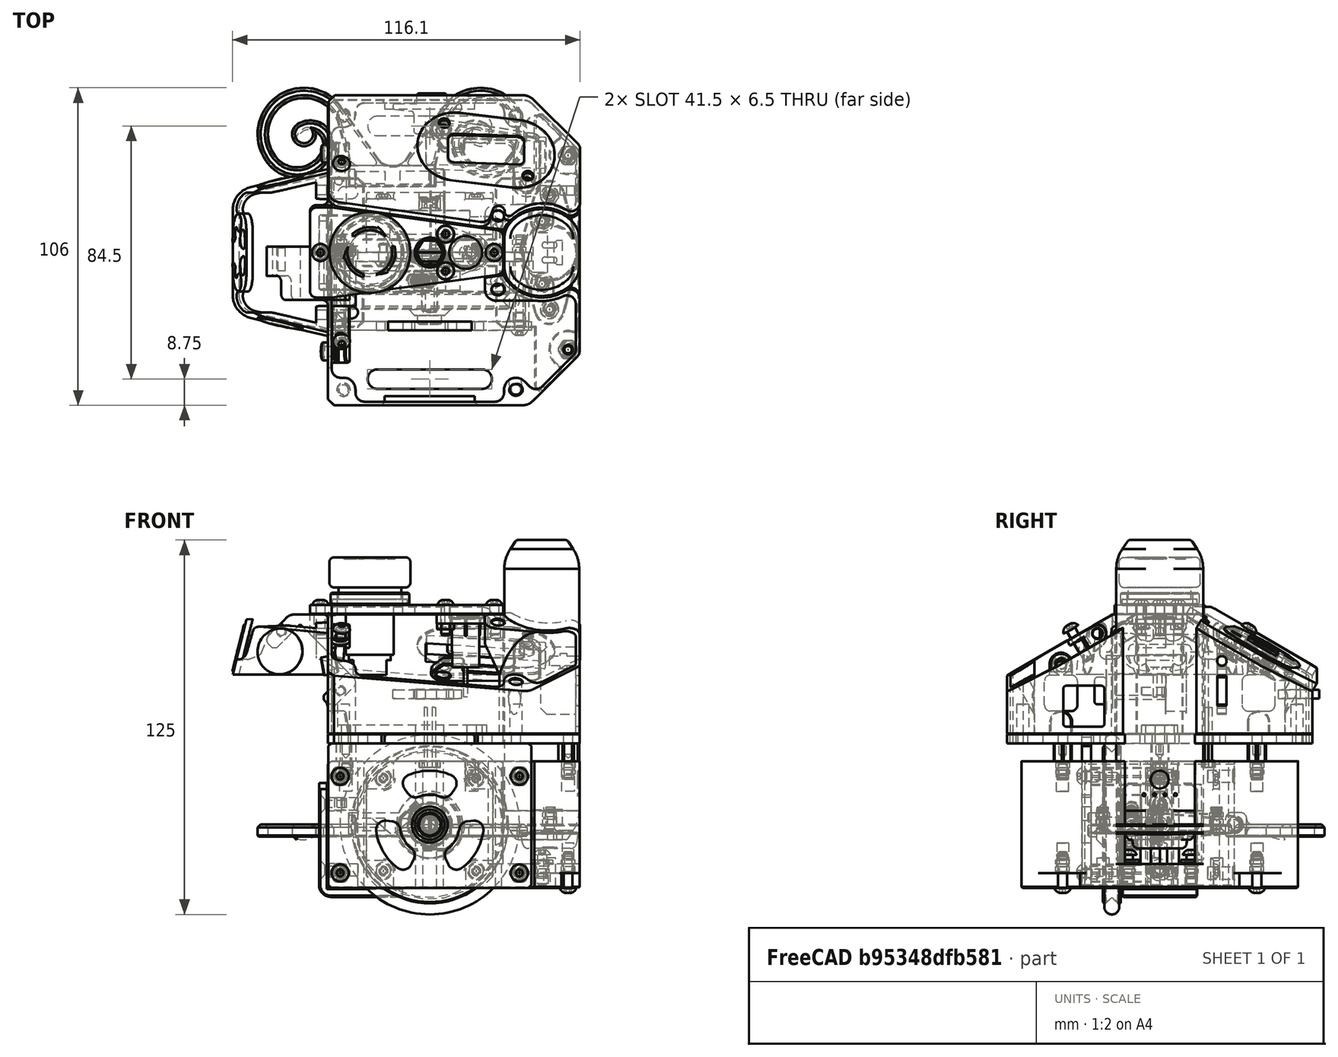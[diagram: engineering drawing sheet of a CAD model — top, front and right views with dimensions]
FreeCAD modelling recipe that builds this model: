
FCSTD DOCUMENT  (FreeCAD 2024.113R14555 (Git shallow))
Label: GridfinityBinPami
License: All rights reserved
LicenseURL: https://en.wikipedia.org/wiki/All_rights_reserved
objects: Part::Feature×86, App::Part×20, PartDesign::Fillet×8, Sketcher::SketchObject×7, PartDesign::Pad×6, App::Link×3, PartDesign::Chamfer×2, PartDesign::LinearPattern×2, PartDesign::Pocket×2, PartDesign::MultiTransform×1, PartDesign::Draft×1, PartDesign::Body×1
note: 167 computed .brp shape members not serialized (recipe doc carries the construction recipe); baked Part::Feature solids carry a one-line shape summary decoded from their .brp

FEATURE [Part::Feature] Solid  label="CarterSuperieur"
  FixShape = 1
  InvalidShape = false
  Placement = pos=(0,0,30.15) rot=(0,0,1;0rad)
  TreeRank = 7
  ValidateShape = false
  shape: bbox 104.5 x 102 x 40 mm, 286 faces (baked)
FEATURE [Part::Feature] Solid001  label="M4-Rondelle"
  FixShape = 1
  InvalidShape = false
  Placement = pos=(12,0,70.15) rot=(1,0,0;3.14159rad)
  TreeRank = 8
  ValidateShape = false
  shape: bbox 9 x 9 x 0.8 mm, 4 faces (baked)
FEATURE [Part::Feature] Solid002  label="TransferCarter"
  FixShape = 1
  InvalidShape = false
  TreeRank = 9
  ValidateShape = false
  shape: bbox 64.5 x 30 x 0.2 mm, 16 faces (baked)
FEATURE [Part::Feature] Solid003  label="BrideReed"
  FixShape = 1
  InvalidShape = false
  Placement = pos=(0,0,70.15) rot=(0,0,1;0rad)
  TreeRank = 10
  ValidateShape = false
  shape: bbox 16.01 x 18.3 x 3 mm, 13 faces (baked)
FEATURE [Part::Feature] Solid004  label="TopCarter"
  FixShape = 1
  InvalidShape = false
  Placement = pos=(0,0,70.35) rot=(0,0,1;0rad)
  TreeRank = 11
  ValidateShape = false
  shape: bbox 64.5 x 30 x 3 mm, 19 faces (baked)
FEATURE [Part::Feature] Solid005  label="BAU"
  FixShape = 1
  InvalidShape = false
  Placement = pos=(-20,0,56.7) rot=(0,0,1;0rad)
  TreeRank = 12
  ValidateShape = false
  shape: bbox 28.6 x 28.6 x 39.3 mm, 42 faces (baked)
FEATURE [Part::Feature] Solid006  label="ReedSensorShort"
  FixShape = 1
  InvalidShape = false
  Placement = pos=(12,0,69.15) rot=(0,0,1;0rad)
  TreeRank = 25
  ValidateShape = false
  shape: bbox 11 x 11 x 26.6 mm, 73 faces (baked)
FEATURE [Part::Feature] Solid007  label="BagueBAU"
  FixShape = 1
  InvalidShape = false
  Placement = pos=(-20,0,73.35) rot=(0,0,1;0rad)
  TreeRank = 26
  ValidateShape = false
  shape: bbox 26.25 x 26.25 x 4 mm, 8 faces (baked)
FEATURE [Part::Feature] Solid008  label="M3x10-Vis"
  FixShape = 1
  InvalidShape = false
  Placement = pos=(-36.5,0,73.35) rot=(0,0,1;0rad)
  TreeRank = 27
  ValidateShape = false
  shape: bbox 5.7 x 5.7 x 11.65 mm, 15 faces (baked)
FEATURE [Part::Feature] Solid009  label="M3x10-Vis004"
  FixShape = 1
  InvalidShape = false
  Placement = pos=(5.29088,-6.14799,73.35) rot=(0,0,1;0rad)
  TreeRank = 28
  ValidateShape = false
  shape: bbox 5.7 x 5.7 x 11.65 mm, 15 faces (baked)
FEATURE [Part::Feature] Solid010  label="M3x10-Vis005"
  FixShape = 1
  InvalidShape = false
  Placement = pos=(5.29088,6.14799,73.35) rot=(0,0,1;0rad)
  TreeRank = 29
  ValidateShape = false
  shape: bbox 5.7 x 5.7 x 11.65 mm, 15 faces (baked)
FEATURE [Part::Feature] Solid011  label="M3x10-Vis006"
  FixShape = 1
  InvalidShape = false
  Placement = pos=(21.5,0,73.35) rot=(0,0,1;0rad)
  TreeRank = 30
  ValidateShape = false
  shape: bbox 5.7 x 5.7 x 11.65 mm, 15 faces (baked)
FEATURE [Part::Feature] Solid012  label="M2.5-Écrou"
  FixShape = 1
  InvalidShape = false
  Placement = pos=(5.29088,6.14799,67.15) rot=(1,0,0;3.14159rad)
  TreeRank = 31
  ValidateShape = false
  shape: bbox 5.774 x 5.774 x 2 mm, 25 faces (baked)
FEATURE [Part::Feature] Solid013  label="M2.5-Écrou001"
  FixShape = 1
  InvalidShape = false
  Placement = pos=(5.29088,-6.14799,67.15) rot=(1,0,0;3.14159rad)
  TreeRank = 32
  ValidateShape = false
  shape: bbox 5.774 x 5.774 x 2 mm, 25 faces (baked)
FEATURE [App::Part] Part  label="VisserieIHM"
  ClaimAllChildren = false
  ExportMode = 1
  Group = -> [Solid008,Solid009,Solid010,Solid011,Solid012,Solid013]
  Origin = -> Origin
  TreeRank = 34
  _ExportChildren = -> [Solid008,Solid009,Solid010,Solid011,Solid012,Solid013]
  _GroupVersion = 1
FEATURE [App::Part] Part001  label="TopIHM"
  ClaimAllChildren = false
  ExportMode = 1
  Group = -> [Solid001,Solid002,Solid003,Solid004,Solid005,Solid006,Solid007,Part]
  Origin = -> Origin001
  TreeRank = 36
  _ExportChildren = -> [Solid001,Solid002,Solid003,Solid004,Solid005,Solid006,Solid007,Part]
  _GroupVersion = 1
FEATURE [Part::Feature] Solid014  label="Rotule"
  FixShape = 1
  InvalidShape = false
  Placement = pos=(-32.8,-20.8,63.8) rot=(1,0,0;0.523599rad)
  TreeRank = 49
  ValidateShape = false
  shape: bbox 6 x 13.59 x 8.169 mm, 29 faces (baked)
FEATURE [Part::Feature] Solid015  label="M3x12-Vis150"
  FixShape = 1
  InvalidShape = false
  Placement = pos=(-29.4979,-29.7083,65.2297) rot=(0.990394,0.138272,0;0.527788rad)
  TreeRank = 50
  ValidateShape = false
  shape: bbox 5.686 x 9.628 x 13.02 mm, 15 faces (baked)
FEATURE [Part::Feature] Solid016  label="M3x12-Vis151"
  FixShape = 1
  InvalidShape = false
  Placement = pos=(-29.4979,29.7083,65.2297) rot=(-0.990394,0.138272,0;0.527788rad)
  TreeRank = 51
  ValidateShape = false
  shape: bbox 5.686 x 9.628 x 13.02 mm, 15 faces (baked)
FEATURE [App::Part] Part002  label="VisserieAiles"
  ClaimAllChildren = false
  ExportMode = 1
  Group = -> [Solid015,Solid016]
  Origin = -> Origin002
  TreeRank = 53
  _ExportChildren = -> [Solid015,Solid016]
  _GroupVersion = 1
FEATURE [Part::Feature] Solid017  label="AileDroite"
  FixShape = 1
  InvalidShape = false
  TreeRank = 54
  ValidateShape = false
  shape: bbox 84.21 x 43.81 x 28.18 mm, 31 faces (baked)
FEATURE [Part::Feature] Solid018  label="CacheEcran"
  FixShape = 1
  InvalidShape = false
  TreeRank = 55
  ValidateShape = false
  shape: bbox 47.84 x 26.64 x 14.69 mm, 36 faces (baked)
FEATURE [Part::Feature] Solid019  label="SupportOled"
  FixShape = 1
  InvalidShape = false
  TreeRank = 56
  ValidateShape = false
  shape: bbox 36.56 x 26.07 x 14.38 mm, 50 faces (baked)
FEATURE [Part::Feature] Solid020  label="ProtectionEcran"
  FixShape = 1
  InvalidShape = false
  TreeRank = 57
  ValidateShape = false
  shape: bbox 45.85 x 25.07 x 13.51 mm, 8 faces (baked)
FEATURE [App::Part] Part003  label="Ailes"
  ClaimAllChildren = false
  ExportMode = 1
  Group = -> [Solid014,Part002,Solid017,Solid018,Solid019,Solid020]
  Origin = -> Origin003
  TreeRank = 59
  _ExportChildren = -> [Solid014,Part002,Solid017,Solid018,Solid019,Solid020]
  _GroupVersion = 1
FEATURE [Part::Feature] Solid021  label="HeadSupport"
  FixShape = 1
  InvalidShape = false
  Placement = pos=(-34,0,70.15) rot=(0,0,1;0rad)
  TreeRank = 60
  ValidateShape = false
  shape: bbox 32.13 x 55.71 x 20.11 mm, 132 faces (baked)
FEATURE [Part::Feature] Solid022  label="Transparent"
  FixShape = 1
  InvalidShape = false
  TreeRank = 76
  ValidateShape = false
  shape: bbox 20.45 x 4.4 x 19.2 mm, 15 faces (baked)
FEATURE [Part::Feature] Solid023  label="SupportColor"
  FixShape = 1
  InvalidShape = false
  TreeRank = 77
  ValidateShape = false
  shape: bbox 15 x 0.2 x 15 mm, 3 faces (baked)
FEATURE [Part::Feature] Solid024  label="Pupille"
  FixShape = 1
  InvalidShape = false
  Placement = pos=(0,-0.4,0.4) rot=(0,0,1;0rad)
  TreeRank = 78
  ValidateShape = false
  shape: bbox 10.82 x 0.8 x 10.82 mm, 4 faces (baked)
FEATURE [App::Part] Part004  label="Eye"
  ClaimAllChildren = false
  ExportMode = 1
  Group = -> [Solid022,Solid023,Solid024]
  Origin = -> Origin004
  Placement = pos=(-49.9835,-23.9284,57.8424) rot=(-0.357536,0.040736,-0.93301;0.243029rad)
  TreeRank = 80
  _ExportChildren = -> [Solid022,Solid023,Solid024]
  _GroupVersion = 1
FEATURE [App::Link] Link  label="Eye001"
  AutoLinkLabel = true
  AutoPlacement = true
  LinkPlacement = pos=(-49.9978,23.9423,57.839) rot=(0.025674,-0.037293,0.998975;3.39991rad)
  LinkedObject = -> Part004
  Placement = pos=(-49.9978,23.9423,57.839) rot=(0.025674,-0.037293,0.998975;3.39991rad)
  SyncGroupVisibility = false
  TreeRank = 81
  _LinkVersion = 1
FEATURE [Part::Feature] Solid025  label="BoutonInter"
  FixShape = 1
  InvalidShape = false
  Placement = pos=(-1.35,49.8,42.05) rot=(0,0,1;0rad)
  TreeRank = 82
  ValidateShape = false
  shape: bbox 23 x 13.5 x 3 mm, 30 faces (baked)
FEATURE [Part::Feature] Solid026  label="SpacerPCB"
  FixShape = 1
  InvalidShape = false
  Placement = pos=(0,0,30.2) rot=(0,0,1;0rad)
  TreeRank = 83
  ValidateShape = false
  shape: bbox 51.45 x 12 x 3.367 mm, 17 faces (baked)
FEATURE [Part::Feature] Solid027  label="DiffuseurLed"
  FixShape = 1
  InvalidShape = false
  TreeRank = 84
  ValidateShape = false
  shape: bbox 13 x 3 x 22.4 mm, 30 faces (baked)
FEATURE [Part::Feature] Solid028  label="Horn"
  FixShape = 1
  InvalidShape = false
  TreeRank = 85
  ValidateShape = false
  shape: bbox 5 x 32.81 x 10 mm, 27 faces (baked)
FEATURE [Part::Feature] Solid029  label="Antennas"
  FixShape = 1
  InvalidShape = false
  Placement = pos=(-12.5,25,0) rot=(0,0,1;0rad)
  TreeRank = 86
  ValidateShape = false
  shape: bbox 90 x 33 x 9.53 mm, 91 faces (baked)
FEATURE [App::Part] Part005  label="EnsembleAntennas"
  ClaimAllChildren = false
  ExportMode = 1
  Group = -> [Solid028,Solid029]
  Origin = -> Origin005
  Placement = pos=(-43.2,14,58.1) rot=(0.540716,0.540716,0.644401;1.99673rad)
  TreeRank = 88
  _ExportChildren = -> [Solid028,Solid029]
  _GroupVersion = 1
FEATURE [App::Part] Part006  label="ChassisSuperieur"
  ClaimAllChildren = false
  ExportMode = 1
  Group = -> [Solid,Part001,Part003,Solid021,Part004,Link,Solid025,Solid026,Solid027,Part005]
  Origin = -> Origin006
  TreeRank = 90
  _ExportChildren = -> [Solid,Part001,Part003,Solid021,Part004,Link,Solid025,Solid026,Solid027,Part005]
  _GroupVersion = 1
FEATURE [Part::Feature] Solid030  label="17HS08-1004S"
  FixShape = 1
  InvalidShape = false
  Placement = pos=(-2.4e-15,20,-4.4e-15) rot=(0,-0.707107,0.707107;3.14159rad)
  TreeRank = 100
  ValidateShape = false
  shape: bbox 42.32 x 40 x 62.15 mm, 316 faces (baked)
FEATURE [Part::Feature] Solid031  label="Roue60mm"
  FixShape = 1
  InvalidShape = false
  Placement = pos=(0,-6,0) rot=(0,0,1;0rad)
  TreeRank = 101
  ValidateShape = false
  shape: bbox 52.53 x 18 x 56.46 mm, 37 faces (baked)
FEATURE [Part::Feature] Solid032  label="JointTorique"
  FixShape = 1
  InvalidShape = false
  Placement = pos=(0,-16,0) rot=(0,0,1;0rad)
  TreeRank = 102
  ValidateShape = false
  shape: bbox 64.94 x 5 x 64.94 mm, 1 faces (baked)
FEATURE [Part::Feature] Solid033  label="M3-Insert004"
  FixShape = 1
  InvalidShape = false
  Placement = pos=(-1e-16,-9.5,-8.1) rot=(0.617822,0.786318,0;3.14159rad)
  TreeRank = 103
  ValidateShape = false
  shape: bbox 4.55 x 4.55 x 5.74 mm, 12 faces (baked)
FEATURE [Part::Feature] Solid034  label="M3-Insert005"
  FixShape = 1
  InvalidShape = false
  Placement = pos=(-5.72756,-9.5,5.72756) rot=(0,-1,0;0.785398rad)
  TreeRank = 104
  ValidateShape = false
  shape: bbox 7.032 x 4.55 x 7.032 mm, 12 faces (baked)
FEATURE [Part::Feature] Solid035  label="M3x3-Screw"
  FixShape = 1
  InvalidShape = false
  Placement = pos=(-5.72756,-9.5,5.72756) rot=(0,-1,0;0.785398rad)
  TreeRank = 105
  ValidateShape = false
  shape: bbox 3.677 x 3 x 3.677 mm, 14 faces (baked)
FEATURE [Part::Feature] Solid036  label="M3x3-Screw001"
  FixShape = 1
  InvalidShape = false
  Placement = pos=(0,-9.5,-8.1) rot=(1,0,0;3.14159rad)
  TreeRank = 106
  ValidateShape = false
  shape: bbox 3 x 3 x 3 mm, 14 faces (baked)
FEATURE [App::Part] Part007  label="VisserieRoue"
  ClaimAllChildren = false
  ExportMode = 1
  Group = -> [Solid033,Solid034,Solid035,Solid036]
  Origin = -> Origin007
  TreeRank = 108
  _ExportChildren = -> [Solid033,Solid034,Solid035,Solid036]
  _GroupVersion = 1
FEATURE [Part::Feature] Compound  label="CoreMF128"
  FixShape = 1
  InvalidShape = false
  TreeRank = 120
  ValidateShape = false
  shape: bbox 13.6 x 3.5 x 13.6 mm, 10 faces, 2 solids (baked)
FEATURE [Part::Feature] Solid037  label="SleeveMF128"
  FixShape = 1
  InvalidShape = false
  TreeRank = 121
  ValidateShape = false
  shape: bbox 11 x 3 x 11 mm, 4 faces (baked)
FEATURE [App::Part] Part008  label="MF128"
  ClaimAllChildren = false
  ExportMode = 1
  Group = -> [Compound,Solid037]
  Origin = -> Origin008
  Placement = pos=(0,-21.8,0) rot=(0,0,1;0rad)
  TreeRank = 123
  _ExportChildren = -> [Compound,Solid037]
  _GroupVersion = 1
FEATURE [App::Part] Part009  label="EnsembleRoue60mm"
  ClaimAllChildren = false
  ExportMode = 1
  Group = -> [Solid031,Solid032,Part007,Part008]
  Origin = -> Origin009
  Placement = pos=(0,-1.3,0) rot=(0,0,1;0rad)
  TreeRank = 125
  _ExportChildren = -> [Solid031,Solid032,Part007,Part008]
  _GroupVersion = 1
FEATURE [Part::Feature] Solid038  label="MotorPlate"
  FixShape = 1
  InvalidShape = false
  TreeRank = 126
  ValidateShape = false
  shape: bbox 67.84 x 3 x 42.3 mm, 19 faces (baked)
FEATURE [Part::Feature] Solid039  label="M3x20xx6-Standoff"
  FixShape = 1
  InvalidShape = false
  Placement = pos=(-29.9195,-3,16.15) rot=(1,0,0;1.5708rad)
  TreeRank = 127
  ValidateShape = false
  shape: bbox 6.582 x 25.9 x 6.17 mm, 30 faces (baked)
FEATURE [Part::Feature] Solid040  label="M3x20xx6-Standoff001"
  FixShape = 1
  InvalidShape = false
  Placement = pos=(29.9195,-3,16.15) rot=(1,0,0;1.5708rad)
  TreeRank = 128
  ValidateShape = false
  shape: bbox 6.582 x 25.9 x 6.17 mm, 30 faces (baked)
FEATURE [Part::Feature] Solid041  label="M3x20xx6-Standoff002"
  FixShape = 1
  InvalidShape = false
  Placement = pos=(29.9195,-3,-16.15) rot=(1,0,0;1.5708rad)
  TreeRank = 129
  ValidateShape = false
  shape: bbox 6.582 x 25.9 x 6.17 mm, 30 faces (baked)
FEATURE [Part::Feature] Solid042  label="M3x20xx6-Standoff003"
  FixShape = 1
  InvalidShape = false
  Placement = pos=(-29.9195,-3,-16.15) rot=(1,0,0;1.5708rad)
  TreeRank = 130
  ValidateShape = false
  shape: bbox 6.582 x 25.9 x 6.17 mm, 30 faces (baked)
FEATURE [Part::Feature] Solid043  label="M3-Insert"
  FixShape = 1
  InvalidShape = false
  Placement = pos=(29.9195,-3.6e-15,16.15) rot=(1,0,0;1.5708rad)
  TreeRank = 141
  ValidateShape = false
  shape: bbox 4.55 x 5.74 x 4.55 mm, 12 faces (baked)
FEATURE [Part::Feature] Solid044  label="M3-Insert001"
  FixShape = 1
  InvalidShape = false
  Placement = pos=(29.9195,3.6e-15,-16.15) rot=(1,0,0;1.5708rad)
  TreeRank = 142
  ValidateShape = false
  shape: bbox 4.55 x 5.74 x 4.55 mm, 12 faces (baked)
FEATURE [Part::Feature] Solid045  label="M3-Insert002"
  FixShape = 1
  InvalidShape = false
  Placement = pos=(-29.9195,-3.6e-15,16.15) rot=(1,0,0;1.5708rad)
  TreeRank = 143
  ValidateShape = false
  shape: bbox 4.55 x 5.74 x 4.55 mm, 12 faces (baked)
FEATURE [Part::Feature] Solid046  label="M3-Insert003"
  FixShape = 1
  InvalidShape = false
  Placement = pos=(-29.9195,3.6e-15,-16.15) rot=(1,0,0;1.5708rad)
  TreeRank = 144
  ValidateShape = false
  shape: bbox 4.55 x 5.74 x 4.55 mm, 12 faces (baked)
FEATURE [Part::Feature] Solid047  label="M3x6-Screw"
  FixShape = 1
  InvalidShape = false
  Placement = pos=(-29.9195,-26,16.15) rot=(1,0,0;1.5708rad)
  TreeRank = 145
  ValidateShape = false
  shape: bbox 5.7 x 7.65 x 5.7 mm, 15 faces (baked)
FEATURE [Part::Feature] Solid048  label="M3x6-Screw032"
  FixShape = 1
  InvalidShape = false
  Placement = pos=(-29.9195,-26,-16.15) rot=(1,0,0;1.5708rad)
  TreeRank = 146
  ValidateShape = false
  shape: bbox 5.7 x 7.65 x 5.7 mm, 15 faces (baked)
FEATURE [Part::Feature] Solid049  label="M3x6-Screw033"
  FixShape = 1
  InvalidShape = false
  Placement = pos=(29.9195,-26,-16.15) rot=(1,0,0;1.5708rad)
  TreeRank = 147
  ValidateShape = false
  shape: bbox 5.7 x 7.65 x 5.7 mm, 15 faces (baked)
FEATURE [Part::Feature] Solid050  label="M3x6-Screw034"
  FixShape = 1
  InvalidShape = false
  Placement = pos=(29.9195,-26,16.15) rot=(1,0,0;1.5708rad)
  TreeRank = 148
  ValidateShape = false
  shape: bbox 5.7 x 7.65 x 5.7 mm, 15 faces (baked)
FEATURE [Part::Feature] Solid051  label="M3x6-Screw007"
  FixShape = 1
  InvalidShape = false
  Placement = pos=(15.5,-3,15.5) rot=(1,0,0;1.5708rad)
  TreeRank = 149
  ValidateShape = false
  shape: bbox 5.7 x 7.65 x 5.7 mm, 15 faces (baked)
FEATURE [Part::Feature] Solid052  label="M3x6-Screw008"
  FixShape = 1
  InvalidShape = false
  Placement = pos=(15.5,-3,-15.5) rot=(1,0,0;1.5708rad)
  TreeRank = 150
  ValidateShape = false
  shape: bbox 5.7 x 7.65 x 5.7 mm, 15 faces (baked)
FEATURE [Part::Feature] Solid053  label="M3x6-Screw009"
  FixShape = 1
  InvalidShape = false
  Placement = pos=(-15.5,-3,-15.5) rot=(1,0,0;1.5708rad)
  TreeRank = 169
  ValidateShape = false
  shape: bbox 5.7 x 7.65 x 5.7 mm, 15 faces (baked)
FEATURE [Part::Feature] Solid054  label="M3x6-Screw010"
  FixShape = 1
  InvalidShape = false
  Placement = pos=(-15.5,-3,15.5) rot=(1,0,0;1.5708rad)
  TreeRank = 170
  ValidateShape = false
  shape: bbox 5.7 x 7.65 x 5.7 mm, 15 faces (baked)
FEATURE [App::Part] Part010  label="Visserie"
  ClaimAllChildren = false
  ExportMode = 1
  Group = -> [Solid039,Solid040,Solid041,Solid042,Solid043,Solid044,Solid045,Solid046,Solid047,Solid048,Solid049,Solid050,Solid051,Solid052,Solid053,Solid054]
  Origin = -> Origin010
  TreeRank = 172
  _ExportChildren = -> [Solid039,Solid040,Solid041,Solid042,Solid043,Solid044,Solid045,Solid046,Solid047,Solid048,Solid049,Solid050,Solid051,Solid052,Solid053,Solid054]
  _GroupVersion = 1
FEATURE [Part::Feature] Solid055  label="WheelPlate"
  FixShape = 1
  InvalidShape = false
  Placement = pos=(0,-23,0) rot=(0,0,1;0rad)
  TreeRank = 173
  ValidateShape = false
  shape: bbox 67.84 x 3 x 51.3 mm, 45 faces (baked)
FEATURE [App::Part] Part011  label="EnsemblePlate"
  ClaimAllChildren = false
  ExportMode = 1
  Group = -> [Solid038,Part010,Solid055]
  Origin = -> Origin011
  TreeRank = 175
  _ExportChildren = -> [Solid038,Part010,Solid055]
  _GroupVersion = 1
FEATURE [App::Part] Part012  label="EnsembleMoteurRoue"
  ClaimAllChildren = false
  ExportMode = 1
  Group = -> [Solid030,Part009,Part011]
  Origin = -> Origin012
  Placement = pos=(0,-25,0) rot=(0,0,1;0rad)
  TreeRank = 177
  _ExportChildren = -> [Solid030,Part009,Part011]
  _GroupVersion = 1
FEATURE [App::Link] Link001  label="EnsembleMoteurRoue001"
  AutoLinkLabel = true
  AutoPlacement = true
  LinkPlacement = pos=(-2.18557e-06,25,0) rot=(0,0,1;3.14159rad)
  LinkedObject = -> Part012
  Placement = pos=(-2.18557e-06,25,0) rot=(0,0,1;3.14159rad)
  SyncGroupVisibility = false
  TreeRank = 178
  _LinkVersion = 1
FEATURE [Part::Feature] Solid056  label="MainBody"
  FixShape = 1
  InvalidShape = false
  Placement = pos=(0,0,-21.15) rot=(0,0,1;0rad)
  TreeRank = 179
  ValidateShape = false
  shape: bbox 84 x 92.34 x 42.3 mm, 166 faces (baked)
FEATURE [Part::Feature] Solid057  label="M3x5.74-Insert"
  FixShape = 1
  InvalidShape = false
  Placement = pos=(46.2,32.426,-15.75) rot=(1,0,0;3.14159rad)
  TreeRank = 180
  ValidateShape = false
  shape: bbox 4.55 x 4.55 x 5.74 mm, 12 faces (baked)
FEATURE [Part::Feature] Solid058  label="M3x5.74-Insert066"
  FixShape = 1
  InvalidShape = false
  Placement = pos=(46.2,-32.426,-15.75) rot=(1,0,0;3.14159rad)
  TreeRank = 181
  ValidateShape = false
  shape: bbox 4.55 x 4.55 x 5.74 mm, 12 faces (baked)
FEATURE [Part::Feature] Solid059  label="Body097"
  FixShape = 1
  InvalidShape = false
  TreeRank = 182
  ValidateShape = false
  shape: bbox 4 x 10 x 10 mm, 12 faces (baked)
FEATURE [Part::Feature] Solid060  label="Body098"
  FixShape = 1
  InvalidShape = false
  TreeRank = 183
  ValidateShape = false
  shape: bbox 3.8 x 8 x 8 mm, 4 faces (baked)
FEATURE [App::Part] Part013  label="623ZZ"
  ClaimAllChildren = false
  ExportMode = 1
  Group = -> [Solid059,Solid060]
  Origin = -> Origin013
  Placement = pos=(46.2,-32.4,-17.15) rot=(0,1,0;1.5708rad)
  TreeRank = 185
  _ExportChildren = -> [Solid059,Solid060]
  _GroupVersion = 1
FEATURE [App::Link] Link002  label="623ZZ001"
  AutoLinkLabel = true
  AutoPlacement = true
  LinkPlacement = pos=(46.2,32.4,-17.15) rot=(0,1,0;1.5708rad)
  LinkedObject = -> Part013
  Placement = pos=(46.2,32.4,-17.15) rot=(0,1,0;1.5708rad)
  SyncGroupVisibility = false
  TreeRank = 186
  _LinkVersion = 1
FEATURE [Part::Feature] Solid061  label="M3x12-Vis"
  FixShape = 1
  InvalidShape = false
  Placement = pos=(46.2,-32.426,-21.15) rot=(1,0,0;3.14159rad)
  TreeRank = 199
  ValidateShape = false
  shape: bbox 5.7 x 5.7 x 13.65 mm, 15 faces (baked)
FEATURE [Part::Feature] Solid062  label="M3x12-Vis152"
  FixShape = 1
  InvalidShape = false
  Placement = pos=(46.2,32.426,-21.15) rot=(1,0,0;3.14159rad)
  TreeRank = 200
  ValidateShape = false
  shape: bbox 5.7 x 5.7 x 13.65 mm, 15 faces (baked)
FEATURE [App::Part] Part014  label="EnsembleRoulements"
  ClaimAllChildren = false
  ExportMode = 1
  Group = -> [Solid057,Solid058,Part013,Link002,Solid061,Solid062]
  Origin = -> Origin014
  TreeRank = 202
  _ExportChildren = -> [Solid057,Solid058,Part013,Link002,Solid061,Solid062]
  _GroupVersion = 1
FEATURE [Part::Feature] Solid063  label="SupportPatin"
  FixShape = 1
  InvalidShape = false
  TreeRank = 203
  ValidateShape = false
  shape: bbox 20 x 48 x 3 mm, 37 faces (baked)
FEATURE [Part::Feature] Solid064  label="Patin"
  FixShape = 1
  InvalidShape = false
  Placement = pos=(40,0,-3) rot=(0,0,1;0rad)
  TreeRank = 204
  ValidateShape = false
  shape: bbox 19.54 x 19.54 x 5 mm, 31 faces (baked)
FEATURE [Part::Feature] Solid065  label="M3x8-Vis"
  FixShape = 1
  InvalidShape = false
  Placement = pos=(40,-19,-3) rot=(1,0,0;3.14159rad)
  TreeRank = 205
  ValidateShape = false
  shape: bbox 6 x 6 x 8 mm, 16 faces (baked)
FEATURE [Part::Feature] Solid066  label="M3x8-Vis001"
  FixShape = 1
  InvalidShape = false
  Placement = pos=(40,19,-3) rot=(1,0,0;3.14159rad)
  TreeRank = 206
  ValidateShape = false
  shape: bbox 6 x 6 x 8 mm, 16 faces (baked)
FEATURE [Part::Feature] Solid067  label="M3x5.74-Insert010"
  FixShape = 1
  InvalidShape = false
  Placement = pos=(40,-19,0) rot=(1,0,0;3.14159rad)
  TreeRank = 207
  ValidateShape = false
  shape: bbox 4.55 x 4.55 x 5.74 mm, 12 faces (baked)
FEATURE [Part::Feature] Solid068  label="M3x5.74-Insert011"
  FixShape = 1
  InvalidShape = false
  Placement = pos=(40,19,0) rot=(1,0,0;3.14159rad)
  TreeRank = 208
  ValidateShape = false
  shape: bbox 4.55 x 4.55 x 5.74 mm, 12 faces (baked)
FEATURE [App::Part] Part015  label="EnsemblePatin"
  ClaimAllChildren = false
  ExportMode = 1
  Group = -> [Solid063,Solid064,Solid065,Solid066,Solid067,Solid068]
  Origin = -> Origin015
  Placement = pos=(0,0,-21.15) rot=(0,0,1;0rad)
  TreeRank = 210
  _ExportChildren = -> [Solid063,Solid064,Solid065,Solid066,Solid067,Solid068]
  _GroupVersion = 1
FEATURE [Part::Feature] Solid069  label="M3x5.74-Insert067"
  FixShape = 1
  InvalidShape = false
  Placement = pos=(46.2,-32.426,20.75) rot=(0,0,1;0rad)
  TreeRank = 221
  ValidateShape = false
  shape: bbox 4.55 x 4.55 x 5.74 mm, 12 faces (baked)
FEATURE [Part::Feature] Solid070  label="M3x5.74-Insert068"
  FixShape = 1
  InvalidShape = false
  Placement = pos=(46.2,32.426,20.75) rot=(0,0,1;0rad)
  TreeRank = 222
  ValidateShape = false
  shape: bbox 4.55 x 4.55 x 5.74 mm, 12 faces (baked)
FEATURE [Part::Feature] Solid071  label="M3x5.74-Insert069"
  FixShape = 1
  InvalidShape = false
  Placement = pos=(-28,0,20.75) rot=(0,0,1;0rad)
  TreeRank = 223
  ValidateShape = false
  shape: bbox 4.55 x 4.55 x 5.74 mm, 12 faces (baked)
FEATURE [Part::Feature] Solid072  label="M3x5.74-Insert070"
  FixShape = 1
  InvalidShape = false
  Placement = pos=(-33.6,0,-15.15) rot=(0,-1,0;1.5708rad)
  TreeRank = 224
  ValidateShape = false
  shape: bbox 5.74 x 4.55 x 4.55 mm, 12 faces (baked)
FEATURE [Part::Feature] Solid073  label="M3x5.74-Insert071"
  FixShape = 1
  InvalidShape = false
  Placement = pos=(-33.6,0,6.85) rot=(0,-1,0;1.5708rad)
  TreeRank = 225
  ValidateShape = false
  shape: bbox 5.74 x 4.55 x 4.55 mm, 12 faces (baked)
FEATURE [Part::Feature] Solid074  label="M3x6xx6-Entretoise filetéé"
  FixShape = 1
  InvalidShape = false
  Placement = pos=(46.2,-32.426,21.15) rot=(0,0,1;0rad)
  TreeRank = 226
  ValidateShape = false
  shape: bbox 6.582 x 6.17 x 11.9 mm, 30 faces (baked)
FEATURE [Part::Feature] Solid075  label="M3x6xx6-Entretoise filetéé001"
  FixShape = 1
  InvalidShape = false
  Placement = pos=(46.2,32.426,21.15) rot=(0,0,1;0rad)
  TreeRank = 227
  ValidateShape = false
  shape: bbox 6.582 x 6.17 x 11.9 mm, 30 faces (baked)
FEATURE [Part::Feature] Solid076  label="M3x6xx6-Entretoise filetéé002"
  FixShape = 1
  InvalidShape = false
  Placement = pos=(-28,0,21.15) rot=(0,0,1;0rad)
  TreeRank = 228
  ValidateShape = false
  shape: bbox 6.582 x 6.17 x 11.9 mm, 30 faces (baked)
FEATURE [Part::Feature] Solid077  label="M3x5.74-Insert072"
  FixShape = 1
  InvalidShape = false
  Placement = pos=(37.5,10.5,-12.2) rot=(0,0,1;0rad)
  TreeRank = 229
  ValidateShape = false
  shape: bbox 4.55 x 4.55 x 5.74 mm, 12 faces (baked)
FEATURE [Part::Feature] Solid078  label="M3x5.74-Insert073"
  FixShape = 1
  InvalidShape = false
  Placement = pos=(37.5,-10.5,-12.2) rot=(0,0,1;0rad)
  TreeRank = 230
  ValidateShape = false
  shape: bbox 4.55 x 4.55 x 5.74 mm, 12 faces (baked)
FEATURE [Part::Feature] Solid079  label="M3x5.74-Insert074"
  FixShape = 1
  InvalidShape = false
  Placement = pos=(14,0,20.75) rot=(0,0,1;0rad)
  TreeRank = 243
  ValidateShape = false
  shape: bbox 4.55 x 4.55 x 5.74 mm, 12 faces (baked)
FEATURE [Part::Feature] Solid080  label="M3x10-Vis007"
  FixShape = 1
  InvalidShape = false
  Placement = pos=(37.5,-10.5,-10.1) rot=(0,0,1;0rad)
  TreeRank = 244
  ValidateShape = false
  shape: bbox 5.7 x 5.7 x 11.65 mm, 15 faces (baked)
FEATURE [Part::Feature] Solid081  label="M3x10-Vis008"
  FixShape = 1
  InvalidShape = false
  Placement = pos=(37.5,10.5,-10.1) rot=(0,0,1;0rad)
  TreeRank = 245
  ValidateShape = false
  shape: bbox 5.7 x 5.7 x 11.65 mm, 15 faces (baked)
FEATURE [App::Part] Part016  label="VisserieBody"
  ClaimAllChildren = false
  ExportMode = 1
  Group = -> [Solid069,Solid070,Solid071,Solid072,Solid073,Solid074,Solid075,Solid076,Solid077,Solid078,Solid079,Solid080,Solid081]
  Origin = -> Origin016
  TreeRank = 247
  _ExportChildren = -> [Solid069,Solid070,Solid071,Solid072,Solid073,Solid074,Solid075,Solid076,Solid077,Solid078,Solid079,Solid080,Solid081]
  _GroupVersion = 1
FEATURE [Part::Feature] Solid082  label="TopPlate"
  FixShape = 1
  InvalidShape = false
  Placement = pos=(0,0,27.15) rot=(0,0,1;0rad)
  TreeRank = 248
  ValidateShape = false
  shape: bbox 84 x 102 x 3 mm, 69 faces (baked)
FEATURE [Part::Feature] Solid083  label="PowerBank-B0BHZ6RY6C"
  FixShape = 1
  InvalidShape = false
  Placement = pos=(37.4,4.7192e-06,-4.99999) rot=(0,0,1;1.5708rad)
  TreeRank = 249
  ValidateShape = false
  shape: bbox 25 x 29.49 x 100 mm, 94 faces (baked)
FEATURE [Part::Feature] Solid084  label="EquerreAvant"
  FixShape = 1
  InvalidShape = false
  Placement = pos=(-34,0,-21.15) rot=(0,0,1;0rad)
  TreeRank = 250
  ValidateShape = false
  shape: bbox 28 x 25 x 38 mm, 30 faces (baked)
FEATURE [App::Part] Part017  label="MotorisationPAMI-V2"
  ClaimAllChildren = false
  ExportMode = 1
  Group = -> [Part012,Link001,Solid056,Part014,Part015,Part016,Solid082,Solid083,Solid084]
  Origin = -> Origin017
  TreeRank = 252
  _ExportChildren = -> [Part012,Link001,Solid056,Part014,Part015,Part016,Solid082,Solid083,Solid084]
  _GroupVersion = 1
FEATURE [App::Part] Part018  label="Pami_2024"
  ClaimAllChildren = false
  ExportMode = 1
  Group = -> [Part006,Part017]
  Origin = -> Origin018
  Placement = pos=(54.5,63,37.3) rot=(0,0,1;3.14159rad)
  TreeRank = 254
  _ExportChildren = -> [Part006,Part017]
  _GroupVersion = 1
FEATURE [Sketcher::SketchObject] Sketch001
  ArcFitTolerance = 1e-06
  AttachmentSupport = -> [XY_Plane001]
  ExternalBSplineMaxDegree = 5
  ExternalBSplineTolerance = 0.0001
  FixShape = 1
  FullyConstrained = true
  InternalTolerance = 1e-06
  InvalidShape = false
  MakeInternals = false
  MapMode = 5
  Support = -> [XY_Plane001]
  TreeRank = 281
  ValidateShape = false
  sketch-geometry (11):
    g0: ArcOfCircle CenterX=4 CenterY=4 CenterZ=0 NormalX=0 NormalY=0 NormalZ=1 AngleXU=0 Radius=3.75 StartAngle=3.14159 EndAngle=4.71239
    g1: LineSegment StartX=0.25 StartY=4 StartZ=0 EndX=0.25 EndY=38 EndZ=0
    g2: ArcOfCircle CenterX=4 CenterY=38 CenterZ=0 NormalX=0 NormalY=0 NormalZ=1 AngleXU=0 Radius=3.75 StartAngle=1.5708 EndAngle=3.14159
    g3: LineSegment StartX=4 StartY=41.75 StartZ=0 EndX=38 EndY=41.75 EndZ=0
    g4: ArcOfCircle CenterX=38 CenterY=38 CenterZ=0 NormalX=0 NormalY=0 NormalZ=1 AngleXU=0 Radius=3.75 StartAngle=3e-16 EndAngle=1.5708
    g5: LineSegment StartX=41.75 StartY=38 StartZ=0 EndX=41.75 EndY=4 EndZ=0
    g6: ArcOfCircle CenterX=38 CenterY=4 CenterZ=0 NormalX=0 NormalY=0 NormalZ=1 AngleXU=0 Radius=3.75 StartAngle=4.71239 EndAngle=6.28319
    g7: LineSegment StartX=38 StartY=0.25 StartZ=0 EndX=4 EndY=0.25 EndZ=0
    g8: GeomPoint [constr] X=0.25 Y=0.25 Z=0
    g9: GeomPoint [constr] X=41.75 Y=41.75 Z=0
    g10: GeomPoint [constr] X=21 Y=21 Z=0
  constraints (25):
    c: Tangent(g0,g1) = 1.5708
    c: Tangent(g1,g2) = 1.5708
    c: Tangent(g2,g3) = 1.5708
    c: Tangent(g3,g4) = 1.5708
    c: Tangent(g4,g5) = 1.5708
    c: Tangent(g5,g6) = 1.5708
    c: Tangent(g6,g7) = 1.5708
    c: Tangent(g7,g0) = 1.5708
    c: Horizontal(g3)
    c: Horizontal(g7)
    c: Vertical(g1)
    c: Vertical(g5)
    c: Equal(g0,g2)
    c: Equal(g2,g4)
    c: Equal(g4,g6)
    c: PointOnObject(g8,g1)
    c: PointOnObject(g8,g7)
    c: PointOnObject(g9,g3)
    c: PointOnObject(g9,g5)
    c: Symmetric(g0,g4,g10)
    c: DistanceX(g-1,g10) = 21
    c: Equal(g7,g1)
    c: Radius(g6) = 3.75
    c: DistanceX(g0,g5) = 41.5
    c: DistanceY(g-1,g10) = 21
FEATURE [PartDesign::Pad] Pad001
  AddSubType = 0
  AlongSketchNormal = false
  AutoTaperInnerAngle = true
  CheckUpToFaceLimits = true
  ClaimChildren = false
  Direction = (0,0,1)
  Fit = 0
  FitJoin = 0
  FixShape = 1
  InnerFit = 0
  InnerFitJoin = 0
  InvalidShape = false
  Length = 4.4
  Length2 = 10
  Linearize = true
  NewSolid = false
  Profile = -> Sketch001
  ReferenceAxis = -> Sketch001 [N_Axis]
  Refine = true
  Reversed = true
  Suppress = false
  TaperInnerAngle = 0
  TaperInnerAngleRev = 0
  TreeRank = 282
  Type = 0
  ValidateShape = true
  _ProfileBasedVersion = 1
FEATURE [Sketcher::SketchObject] Sketch002
  ArcFitTolerance = 1e-06
  AttachmentSupport = -> [Pad001]
  ExternalBSplineMaxDegree = 5
  ExternalBSplineTolerance = 0.0001
  FixShape = 1
  FullyConstrained = true
  InternalTolerance = 1e-06
  InvalidShape = false
  MakeInternals = false
  MapMode = 5
  Placement = pos=(0,0,-4.4) rot=(1,0,0;3.14159rad)
  Support = -> [Pad001]
  TreeRank = 283
  ValidateShape = false
  sketch-geometry (11):
    g0: ArcOfCircle CenterX=4 CenterY=-4 CenterZ=0 NormalX=0 NormalY=0 NormalZ=1 AngleXU=0 Radius=1.6 StartAngle=1.5708 EndAngle=3.14159
    g1: LineSegment StartX=4 StartY=-2.4 StartZ=0 EndX=38 EndY=-2.4 EndZ=0
    g2: ArcOfCircle CenterX=38 CenterY=-4 CenterZ=0 NormalX=0 NormalY=0 NormalZ=1 AngleXU=0 Radius=1.6 StartAngle=0 EndAngle=1.5708
    g3: LineSegment StartX=39.6 StartY=-4 StartZ=0 EndX=39.6 EndY=-38 EndZ=0
    g4: ArcOfCircle CenterX=38 CenterY=-38 CenterZ=0 NormalX=0 NormalY=0 NormalZ=1 AngleXU=0 Radius=1.6 StartAngle=4.71239 EndAngle=6.28319
    g5: LineSegment StartX=38 StartY=-39.6 StartZ=0 EndX=4 EndY=-39.6 EndZ=0
    g6: ArcOfCircle CenterX=4 CenterY=-38 CenterZ=0 NormalX=0 NormalY=0 NormalZ=1 AngleXU=0 Radius=1.6 StartAngle=3.14159 EndAngle=4.71239
    g7: LineSegment StartX=2.4 StartY=-38 StartZ=0 EndX=2.4 EndY=-4 EndZ=0
    g8: GeomPoint [constr] X=2.4 Y=-2.4 Z=0
    g9: GeomPoint [constr] X=39.6 Y=-39.6 Z=0
    g10: GeomPoint [constr] X=21 Y=-21 Z=0
  constraints (25):
    c: Tangent(g0,g1) = 1.5708
    c: Tangent(g1,g2) = 1.5708
    c: Tangent(g2,g3) = 1.5708
    c: Tangent(g3,g4) = 1.5708
    c: Tangent(g4,g5) = 1.5708
    c: Tangent(g5,g6) = 1.5708
    c: Tangent(g6,g7) = 1.5708
    c: Tangent(g7,g0) = 1.5708
    c: Horizontal(g1)
    c: Horizontal(g5)
    c: Vertical(g3)
    c: Vertical(g7)
    c: Equal(g0,g2)
    c: Equal(g2,g4)
    c: Equal(g4,g6)
    c: PointOnObject(g8,g1)
    c: PointOnObject(g8,g7)
    c: PointOnObject(g9,g3)
    c: PointOnObject(g9,g5)
    c: Equal(g1,g3)
    c: Symmetric(g0,g4,g10)
    c: Radius(g2) = 1.6
    c: DistanceY(g10,g-1) = 21
    c: DistanceX(g-1,g10) = 21
    c: DistanceX(g0,g2) = 37.2
FEATURE [PartDesign::Pad] Pad002
  AddSubType = 0
  AlongSketchNormal = false
  AutoTaperInnerAngle = true
  BaseFeature = -> Pad001
  CheckUpToFaceLimits = true
  ClaimChildren = false
  Direction = (0,0,-1)
  Fit = 0
  FitJoin = 0
  FixShape = 1
  InnerFit = 0
  InnerFitJoin = 0
  InvalidShape = false
  Length = 2.6
  Length2 = 10
  Linearize = true
  NewSolid = false
  Profile = -> Sketch002
  ReferenceAxis = -> Sketch002 [N_Axis]
  Refine = true
  Suppress = false
  TaperInnerAngle = 0
  TaperInnerAngleRev = 0
  TreeRank = 284
  Type = 0
  ValidateShape = true
  _ProfileBasedVersion = 1
FEATURE [PartDesign::Chamfer] Chamfer
  AddSubType = 0
  Angle = 45
  Base = -> Pad002 [Edge37]
  BaseFeature = -> Pad002
  ChamferType = 0
  FixShape = 1
  FlipDirection = false
  InvalidShape = false
  NewSolid = false
  Refine = true
  Size = 0.8
  Size2 = 1
  SupportTransform = false
  Suppress = false
  TreeRank = 285
  UseAllEdges = false
  ValidateShape = true
FEATURE [PartDesign::Chamfer] Chamfer001
  AddSubType = 0
  Angle = 45
  Base = -> Chamfer [Edge15]
  BaseFeature = -> Chamfer
  ChamferType = 0
  FixShape = 1
  FlipDirection = false
  InvalidShape = false
  NewSolid = false
  Refine = true
  Size = 2.149
  Size2 = 1
  SupportTransform = false
  Suppress = false
  TreeRank = 286
  UseAllEdges = false
  ValidateShape = true
FEATURE [PartDesign::LinearPattern] LinearPattern
  AddSubType = 0
  CopyShape = false
  Direction = -> Sketch001 [H_Axis]
  FixShape = 1
  InvalidShape = false
  Length = 84
  NewSolid = false
  Occurrences = 3
  ParallelTransform = true
  Refine = true
  SubTransform = true
  Suppress = false
  TreeRank = 288
  ValidateShape = true
  _Version = 3
FEATURE [PartDesign::LinearPattern] LinearPattern001
  AddSubType = 0
  CopyShape = false
  Direction = -> Sketch001 [V_Axis]
  FixShape = 1
  InvalidShape = false
  Length = 84
  NewSolid = false
  Occurrences = 3
  ParallelTransform = true
  Refine = true
  SubTransform = true
  Suppress = false
  TreeRank = 289
  ValidateShape = true
  _Version = 3
FEATURE [PartDesign::MultiTransform] MultiTransform
  AddSubType = 0
  BaseFeature = -> Chamfer001
  CopyShape = false
  FixShape = 1
  InvalidShape = false
  NewSolid = false
  OriginalSubs = -> [Pad001,Pad002,Chamfer,Chamfer001]
  Originals = -> [Pad001,Pad002,Chamfer,Chamfer001]
  ParallelTransform = true
  Refine = true
  SubTransform = true
  Suppress = false
  Transformations = -> [LinearPattern,LinearPattern001]
  TreeRank = 287
  ValidateShape = true
  _Version = 3
FEATURE [Sketcher::SketchObject] Sketch003
  ArcFitTolerance = 1e-06
  AttachmentSupport = -> [XY_Plane001]
  ExternalBSplineMaxDegree = 5
  ExternalBSplineTolerance = 0.0001
  FixShape = 1
  FullyConstrained = true
  InternalTolerance = 1e-06
  InvalidShape = false
  MakeInternals = false
  MapMode = 5
  Support = -> [XY_Plane001]
  TreeRank = 290
  ValidateShape = false
  sketch-geometry (8):
    g0: LineSegment StartX=84 StartY=126 StartZ=0 EndX=126 EndY=126 EndZ=0
    g1: LineSegment StartX=126 StartY=126 StartZ=0 EndX=126 EndY=84 EndZ=0
    g2: LineSegment StartX=126 StartY=84 StartZ=0 EndX=84 EndY=84 EndZ=0
    g3: LineSegment StartX=84 StartY=84 StartZ=0 EndX=84 EndY=126 EndZ=0
    g4: LineSegment StartX=84 StartY=42 StartZ=0 EndX=126 EndY=42 EndZ=0
    g5: LineSegment StartX=126 StartY=42 StartZ=0 EndX=126 EndY=0 EndZ=0
    g6: LineSegment StartX=126 StartY=0 StartZ=0 EndX=84 EndY=0 EndZ=0
    g7: LineSegment StartX=84 StartY=0 StartZ=0 EndX=84 EndY=42 EndZ=0
  constraints (24):
    c: Coincident(g0,g1)
    c: Coincident(g1,g2)
    c: Coincident(g2,g3)
    c: Coincident(g3,g0)
    c: Horizontal(g0)
    c: Horizontal(g2)
    c: Vertical(g1)
    c: Vertical(g3)
    c: Coincident(g4,g5)
    c: Coincident(g5,g6)
    c: Coincident(g6,g7)
    c: Coincident(g7,g4)
    c: Horizontal(g4)
    c: Horizontal(g6)
    c: Vertical(g5)
    c: Vertical(g7)
    c: Equal(g4,g5)
    c: Equal(g5,g2)
    c: Equal(g2,g1)
    c: DistanceY(g1,g1) = 42
    c: PointOnObject(g5,g-1)
    c: PointOnObject(g4,g1)
    c: DistanceX(g-1,g5) = 126
    c: DistanceY(g5,g0) = 126
FEATURE [PartDesign::Pocket] Pocket
  AddSubType = 1
  AlongSketchNormal = false
  AutoTaperInnerAngle = true
  BaseFeature = -> MultiTransform
  CheckUpToFaceLimits = true
  ClaimChildren = false
  Direction = (0,0,-1)
  Fit = 0
  FitJoin = 0
  FixShape = 1
  InnerFit = 0
  InnerFitJoin = 0
  InvalidShape = false
  Length = 5
  Length2 = 10
  Linearize = true
  NewSolid = false
  Profile = -> Sketch003
  ReferenceAxis = -> Sketch003 [N_Axis]
  Refine = true
  Suppress = false
  TaperInnerAngle = 0
  TaperInnerAngleRev = 0
  TreeRank = 291
  Type = 1
  ValidateShape = true
  _ProfileBasedVersion = 1
  _Version = 1
FEATURE [Sketcher::SketchObject] Sketch004
  ArcFitTolerance = 1e-06
  AttachmentSupport = -> [XY_Plane001]
  ExternalBSplineMaxDegree = 5
  ExternalBSplineTolerance = 0.0001
  FixShape = 1
  FullyConstrained = true
  InternalTolerance = 1e-06
  InvalidShape = false
  MakeInternals = false
  MapMode = 5
  Support = -> [XY_Plane001]
  TreeRank = 292
  ValidateShape = false
  sketch-geometry (6):
    g0: LineSegment StartX=0 StartY=0 StartZ=0 EndX=0 EndY=126 EndZ=0
    g1: LineSegment StartX=0 StartY=126 StartZ=0 EndX=84 EndY=126 EndZ=0
    g2: LineSegment StartX=84 StartY=126 StartZ=0 EndX=126 EndY=84 EndZ=0
    g3: LineSegment StartX=126 StartY=84 StartZ=0 EndX=126 EndY=42 EndZ=0
    g4: LineSegment StartX=126 StartY=42 StartZ=0 EndX=84 EndY=0 EndZ=0
    g5: LineSegment StartX=84 StartY=0 StartZ=0 EndX=0 EndY=0 EndZ=0
  constraints (17):
    c: Coincident(g-1,g0)
    c: PointOnObject(g0,g-2)
    c: Coincident(g0,g1)
    c: Horizontal(g1)
    c: Coincident(g1,g2)
    c: Coincident(g2,g3)
    c: Vertical(g3)
    c: Coincident(g3,g4)
    c: PointOnObject(g4,g-1)
    c: Coincident(g4,g5)
    c: Coincident(g5,g0)
    c: DistanceY(g0,g0) = 126
    c: DistanceY(g3,g3) = 42
    c: DistanceX(g1,g1) = 84
    c: Equal(g5,g1)
    c: Equal(g4,g2)
    c: DistanceX(g0,g2) = 126
FEATURE [PartDesign::Pad] Pad003
  AddSubType = 0
  AlongSketchNormal = false
  AutoTaperInnerAngle = true
  BaseFeature = -> Pocket
  CheckUpToFaceLimits = true
  ClaimChildren = false
  Direction = (0,0,1)
  Fit = -0.1
  FitJoin = 0
  FixShape = 1
  InnerFit = 0
  InnerFitJoin = 0
  InvalidShape = false
  Length = 56
  Length2 = 10
  Linearize = true
  NewSolid = false
  Profile = -> Sketch004
  ReferenceAxis = -> Sketch004 [N_Axis]
  Refine = true
  Suppress = false
  TaperInnerAngle = 0
  TaperInnerAngleRev = 0
  TreeRank = 293
  Type = 0
  ValidateShape = true
  _ProfileBasedVersion = 1
FEATURE [PartDesign::Fillet] Fillet
  AddSubType = 0
  Base = -> Pad003 [Edge73,Edge74]
  BaseFeature = -> Pad003
  FixShape = 1
  InvalidShape = false
  NewSolid = false
  Radius = 4
  Refine = true
  SupportTransform = false
  Suppress = false
  TreeRank = 294
  UseAllEdges = false
  ValidateShape = true
FEATURE [PartDesign::Fillet] Fillet001
  AddSubType = 0
  Base = -> Fillet [Edge72,Edge76,Edge78,Edge74]
  BaseFeature = -> Fillet
  FixShape = 1
  InvalidShape = false
  NewSolid = false
  Radius = 9.5
  Refine = true
  SupportTransform = false
  Suppress = false
  TreeRank = 295
  UseAllEdges = false
  ValidateShape = true
FEATURE [PartDesign::Pocket] Pocket001
  AddSubType = 1
  AlongSketchNormal = false
  AutoTaperInnerAngle = true
  BaseFeature = -> Fillet001
  CheckUpToFaceLimits = true
  ClaimChildren = false
  Direction = (0,0,-1)
  Fit = -2
  FitJoin = 0
  FixShape = 1
  InnerFit = 0
  InnerFitJoin = 0
  InvalidShape = false
  Length = 53
  Length2 = 10
  Linearize = true
  NewSolid = false
  Profile = -> Fillet001 [Face70]
  Refine = true
  Suppress = false
  TaperInnerAngle = 0
  TaperInnerAngleRev = 0
  TreeRank = 296
  Type = 0
  ValidateShape = true
  _ProfileBasedVersion = 1
  _Version = 1
FEATURE [Sketcher::SketchObject] Sketch005
  ArcFitTolerance = 1e-06
  AttachmentSupport = -> [Pocket001]
  ExternalBSplineMaxDegree = 5
  ExternalBSplineTolerance = 0.0001
  FixShape = 1
  FullyConstrained = true
  InternalTolerance = 1e-06
  InvalidShape = false
  MakeInternals = false
  MapMode = 5
  Placement = pos=(0,0,3) rot=(0,0,1;0rad)
  Support = -> [Pocket001]
  TreeRank = 297
  ValidateShape = false
  sketch-geometry (6):
    g0: LineSegment StartX=2 StartY=103 StartZ=0 EndX=124 EndY=84 EndZ=0
    g1: LineSegment StartX=124 StartY=84 StartZ=0 EndX=124 EndY=42 EndZ=0
    g2: LineSegment StartX=124 StartY=42 StartZ=0 EndX=2 EndY=23 EndZ=0
    g3: LineSegment StartX=2 StartY=23 StartZ=0 EndX=2 EndY=103 EndZ=0
    g4: Circle CenterX=14.5 CenterY=63 CenterZ=0 NormalX=0 NormalY=0 NormalZ=1 AngleXU=0 Radius=11
    g5: Circle CenterX=76.5 CenterY=63 CenterZ=0 NormalX=0 NormalY=0 NormalZ=1 AngleXU=0 Radius=11
  constraints (18):
    c: Coincident(g0,g1)
    c: Coincident(g1,g2)
    c: Coincident(g2,g3)
    c: Coincident(g3,g0)
    c: Vertical(g1)
    c: Vertical(g3)
    c: DistanceY(g1,g1) = 42
    c: DistanceY(g1) = 42
    c: Equal(g0,g2)
    c: DistanceY(g3,g3) = 80
    c: Equal(g4,g5)
    c: Diameter(g4) = 22
    c: Horizontal(g4,g5)
    c: DistanceY(g4) = 63
    c: DistanceX(g4,g5) = 62
    c: DistanceX(g-1,g4) = 14.5
    c: DistanceX(g-1,g1) = 124
    c: DistanceX(g-1,g2) = 2
FEATURE [PartDesign::Pad] Pad004
  AddSubType = 0
  AlongSketchNormal = false
  AutoTaperInnerAngle = true
  BaseFeature = -> Pocket001
  CheckUpToFaceLimits = true
  ClaimChildren = false
  Direction = (0,0,1)
  Fit = 0
  FitJoin = 0
  FixShape = 1
  InnerFit = 0
  InnerFitJoin = 0
  InvalidShape = false
  Length = 10
  Length2 = 10
  Linearize = true
  NewSolid = false
  Profile = -> Sketch005
  ReferenceAxis = -> Sketch005 [N_Axis]
  Refine = true
  Suppress = false
  TaperInnerAngle = 0
  TaperInnerAngleRev = 0
  TreeRank = 298
  Type = 0
  ValidateShape = true
  _ProfileBasedVersion = 1
FEATURE [Sketcher::SketchObject] Sketch006
  ArcFitTolerance = 1e-06
  AttachmentSupport = -> [XY_Plane001]
  ExternalBSplineMaxDegree = 5
  ExternalBSplineTolerance = 0.0001
  ExternalGeometry = -> [Pad004]
  FixShape = 1
  FullyConstrained = true
  InternalTolerance = 1e-06
  InvalidShape = false
  MakeInternals = false
  MapMode = 5
  Support = -> [XY_Plane001]
  TreeRank = 299
  ValidateShape = false
  sketch-geometry (4):
    g0: LineSegment StartX=92 StartY=37.0164 StartZ=0 EndX=92 EndY=88.9836 EndZ=0
    g1: LineSegment StartX=92 StartY=88.9836 StartZ=0 EndX=124 EndY=84 EndZ=0
    g2: LineSegment StartX=124 StartY=84 StartZ=0 EndX=124 EndY=42 EndZ=0
    g3: LineSegment StartX=124 StartY=42 StartZ=0 EndX=92 EndY=37.0164 EndZ=0
  constraints (12):
    c: Vertical(g0)
    c: Coincident(g0,g1)
    c: Coincident(g1,g2)
    c: Vertical(g2)
    c: Coincident(g2,g3)
    c: Coincident(g3,g0)
    c: DistanceX(g-1,g2) = 124
    c: DistanceX(g0,g1) = 32
    c: PointOnObject(g1,g-3)
    c: PointOnObject(g0,g-3)
    c: PointOnObject(g2,g-4)
    c: PointOnObject(g0,g-4)
FEATURE [PartDesign::Pad] Pad005
  AddSubType = 0
  AlongSketchNormal = false
  AutoTaperInnerAngle = true
  BaseFeature = -> Pad004
  CheckUpToFaceLimits = true
  ClaimChildren = false
  Direction = (0,0,1)
  Fit = 0
  FitJoin = 0
  FixShape = 1
  InnerFit = 0
  InnerFitJoin = 0
  InvalidShape = false
  Length = 22
  Length2 = 10
  Linearize = true
  NewSolid = false
  Profile = -> Sketch006
  ReferenceAxis = -> Sketch006 [N_Axis]
  Refine = true
  Suppress = false
  TaperInnerAngle = 0
  TaperInnerAngleRev = 0
  TreeRank = 300
  Type = 0
  ValidateShape = true
  _ProfileBasedVersion = 1
FEATURE [PartDesign::Draft] Draft
  AddSubType = 0
  Angle = 10
  Base = -> Pad005 [Face30]
  BaseFeature = -> Pad005
  FixShape = 1
  InvalidShape = false
  NeutralPlane = -> Pad005 [Face28]
  NewSolid = false
  Refine = true
  SupportTransform = false
  Suppress = false
  TreeRank = 301
  ValidateShape = true
FEATURE [PartDesign::Fillet] Fillet002
  AddSubType = 0
  Base = -> Draft [Edge88]
  BaseFeature = -> Draft
  FixShape = 1
  InvalidShape = false
  NewSolid = false
  Radius = 5
  Refine = true
  SupportTransform = false
  Suppress = false
  TreeRank = 302
  UseAllEdges = false
  ValidateShape = true
FEATURE [PartDesign::Fillet] Fillet003
  AddSubType = 0
  Base = -> Fillet002 [Edge29]
  BaseFeature = -> Fillet002
  FixShape = 1
  InvalidShape = false
  NewSolid = false
  Radius = 1
  Refine = true
  SupportTransform = false
  Suppress = false
  TreeRank = 303
  UseAllEdges = false
  ValidateShape = true
FEATURE [PartDesign::Fillet] Fillet004
  AddSubType = 0
  Base = -> Fillet003 [Edge18,Edge19,Edge41,Edge43]
  BaseFeature = -> Fillet003
  FixShape = 1
  InvalidShape = false
  NewSolid = false
  Radius = 1
  Refine = true
  SupportTransform = false
  Suppress = false
  TreeRank = 304
  UseAllEdges = false
  ValidateShape = true
FEATURE [Sketcher::SketchObject] Sketch007
  ArcFitTolerance = 1e-06
  AttachmentSupport = -> [XY_Plane001]
  ExternalBSplineMaxDegree = 5
  ExternalBSplineTolerance = 0.0001
  ExternalGeometry = -> [Fillet004]
  FixShape = 1
  FullyConstrained = true
  InternalTolerance = 1e-06
  InvalidShape = false
  MakeInternals = false
  MapMode = 5
  Support = -> [XY_Plane001]
  TreeRank = 305
  ValidateShape = false
  sketch-geometry (4):
    g0: LineSegment StartX=29 StartY=98.7951 StartZ=0 EndX=29 EndY=27.2049 EndZ=0
    g1: LineSegment StartX=62 StartY=93.6557 StartZ=0 EndX=62 EndY=32.3443 EndZ=0
    g2: LineSegment StartX=29 StartY=98.7951 StartZ=0 EndX=62 EndY=93.6557 EndZ=0
    g3: LineSegment StartX=62 StartY=32.3443 StartZ=0 EndX=29 EndY=27.2049 EndZ=0
  constraints (12):
    c: Vertical(g0)
    c: Vertical(g1)
    c: Coincident(g2,g0)
    c: Coincident(g3,g1)
    c: Coincident(g3,g0)
    c: Coincident(g1,g2)
    c: DistanceX(g-1,g0) = 29
    c: DistanceX(g-1,g1) = 62
    c: PointOnObject(g1,g-4)
    c: PointOnObject(g1,g-3)
    c: PointOnObject(g0,g-3)
    c: PointOnObject(g0,g-4)
FEATURE [PartDesign::Pad] Pad006
  AddSubType = 0
  AlongSketchNormal = false
  AutoTaperInnerAngle = true
  BaseFeature = -> Fillet004
  CheckUpToFaceLimits = true
  ClaimChildren = false
  Direction = (0,0,1)
  Fit = 0
  FitJoin = 0
  FixShape = 1
  InnerFit = 0
  InnerFitJoin = 0
  InvalidShape = false
  Length = 16
  Length2 = 10
  Linearize = true
  NewSolid = false
  Profile = -> Sketch007
  ReferenceAxis = -> Sketch007 [N_Axis]
  Refine = true
  Suppress = false
  TaperInnerAngle = 0
  TaperInnerAngleRev = 0
  TreeRank = 306
  Type = 0
  ValidateShape = true
  _ProfileBasedVersion = 1
FEATURE [PartDesign::Fillet] Fillet005
  AddSubType = 0
  Base = -> Pad006 [Edge15,Edge34,Edge7,Edge10]
  BaseFeature = -> Pad006
  FixShape = 1
  InvalidShape = false
  NewSolid = false
  Radius = 1
  Refine = true
  SupportTransform = false
  Suppress = false
  TreeRank = 307
  UseAllEdges = false
  ValidateShape = true
FEATURE [PartDesign::Fillet] Fillet006
  AddSubType = 0
  Base = -> Fillet005 [Edge12,Edge32]
  BaseFeature = -> Fillet005
  FixShape = 1
  InvalidShape = false
  NewSolid = false
  Radius = 1
  Refine = true
  SupportTransform = false
  Suppress = false
  TreeRank = 308
  UseAllEdges = false
  ValidateShape = true
FEATURE [PartDesign::Fillet] Fillet007
  AddSubType = 0
  Base = -> Fillet006 [Edge3,Edge28]
  BaseFeature = -> Fillet006
  FixShape = 1
  InvalidShape = false
  NewSolid = false
  Radius = 4
  Refine = true
  SupportTransform = false
  Suppress = false
  TreeRank = 309
  UseAllEdges = false
  ValidateShape = true
FEATURE [PartDesign::Body] Body001  label="BinPami"
  AutoGroupSolids = false
  ClaimAllChildren = false
  ExportMode = 0
  FixShape = 1
  Group = -> [Sketch001,Pad001,Sketch002,Pad002,Chamfer,Chamfer001,MultiTransform,LinearPattern,LinearPattern001,Sketch003,Pocket,Sketch004,Pad003,Fillet,Fillet001,Pocket001,Sketch005,Pad004,Sketch006,Pad005,Draft,Fillet002,Fillet003,Fillet004,Sketch007,Pad006,Fillet005,Fillet006,Fillet007]
  InvalidShape = false
  Origin = -> Origin021
  Tip = -> Fillet007
  TreeRank = 280
  ValidateShape = false
  _ExportChildren = -> [Pad001,Pad002,Chamfer,Chamfer001,MultiTransform,Pocket,Pad003,Fillet,Fillet001,Pocket001,Pad004,Pad005,Draft,Fillet002,Fillet003,Fillet004,Pad006,Fillet005,Fillet006,Fillet007]
  _GroupVersion = 1
FEATURE [App::Part] Part019  label="BinPamiAssembly"
  ClaimAllChildren = false
  ExportMode = 1
  Group = -> [Part018,Body001]
  Origin = -> Origin020
  TreeRank = 270
  _ExportChildren = -> [Part018,Body001]
  _GroupVersion = 1
